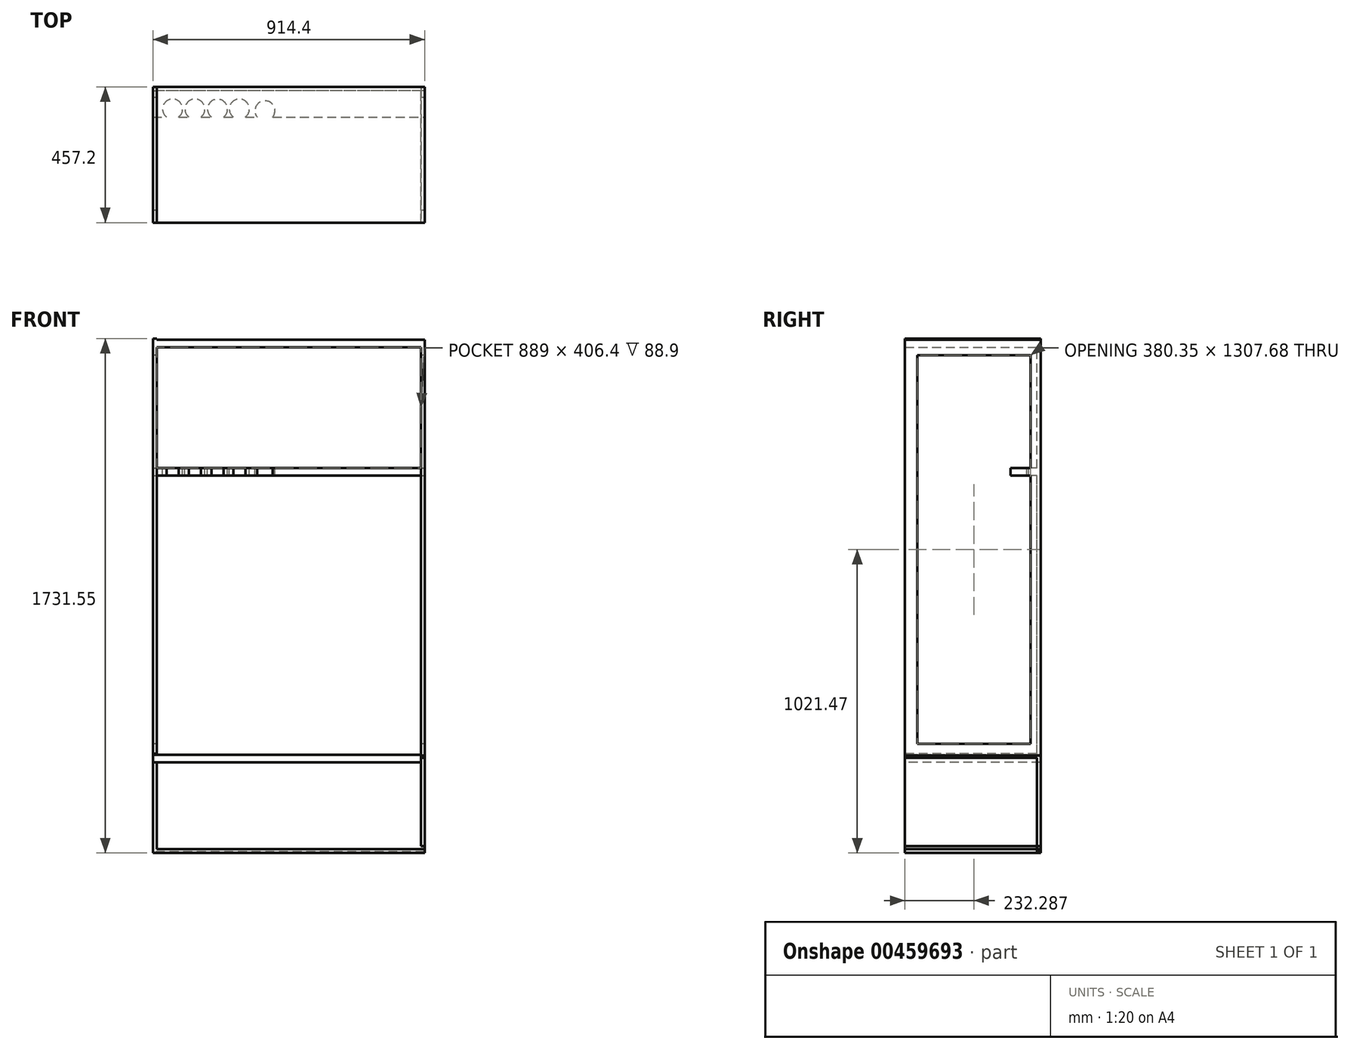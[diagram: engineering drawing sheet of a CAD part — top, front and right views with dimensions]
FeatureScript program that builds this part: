
annotation { "Feature Type Name" : "Feature", "Feature Type Description" : "" }
export const myFeature = defineFeature(function(context is Context, id is Id, definition is map)
    precondition{}
    {
        {
            var Q0;
            Q0=qCreatedBy(makeId("Top.planeOp"),FACE);
            var sketch = newSketch(context, id + "F0", { "sketchPlane" : qUnion([Q0])});
            skLineSegment(sketch, "E0.bottom", {"start": v(0, 0) * mm, "end": v(914.4, 0) * mm});
            skLineSegment(sketch, "E0.top", {"start": v(0, -457.2) * mm, "end": v(914.4, -457.2) * mm});
            skLineSegment(sketch, "E0.left", {"start": v(0, 0) * mm, "end": v(0, -457.2) * mm});
            skLineSegment(sketch, "E0.right", {"start": v(914.4, 0) * mm, "end": v(914.4, -457.2) * mm});
            skSolve(sketch);
        }
        {
            var Q0;
            Q0=makeQuery(id+"F0.imprint","IMPRINT",FACE,{"disambiguationData":[TD([[makeQuery(id+"F0.imprint","IMPRINT",EDGE,{"derivedFrom":sQuery(id+"F0.wireOp",EDGE,"E0.bottom")}),-1.0]])]});
            extrude(context, id + "F1", {"entities" : qUnion([Q0]), "depth" : 12.7 * mm});
        }
        {
            var Q0;
            Q0=qCreatedBy(makeId("Right.planeOp"),FACE);
            var sketch = newSketch(context, id + "F2", { "sketchPlane" : qUnion([Q0])});
            skLineSegment(sketch, "E1.bottom", {"start": v(0, 0) * mm, "end": v(-457.2, 0) * mm});
            skLineSegment(sketch, "E1.top", {"start": v(0, 304.8) * mm, "end": v(-457.2, 304.8) * mm});
            skLineSegment(sketch, "E1.left", {"start": v(0, 0) * mm, "end": v(0, 304.8) * mm});
            skLineSegment(sketch, "E1.right", {"start": v(-457.2, 0) * mm, "end": v(-457.2, 304.8) * mm});
            skSolve(sketch);
        }
        {
            var Q0;
            Q0=makeQuery(id+"F2.imprint","IMPRINT",FACE,{"disambiguationData":[TD([[makeQuery(id+"F2.imprint","IMPRINT",EDGE,{"derivedFrom":sQuery(id+"F2.wireOp",EDGE,"E1.bottom")}),-1.0]])]});
            extrude(context, id + "F3", {"entities" : qUnion([Q0]), "operationType" : NewBodyOperationType.ADD, "depth" : 12.7 * mm});
        }
        {
            var Q0;
            Q0=qCreatedBy(makeId("Right.planeOp"),FACE);
            cPlane(context, id + "F4", {"entities" : qUnion([Q0]), "cplaneType" : CPlaneType.OFFSET, "offset" : 914.4 * mm, "width" : 152.4 * mm, "height" : 152.4 * mm});
        }
        {
            var Q0;
            Q0=qCreatedBy(id+"F4.planeOp",FACE);
            var sketch = newSketch(context, id + "F5", { "sketchPlane" : qUnion([Q0])});
            skLineSegment(sketch, "E2.bottom", {"start": v(-457.2, 23.7) * mm, "end": v(0, 23.7) * mm});
            skLineSegment(sketch, "E2.top", {"start": v(-457.2, 328.5) * mm, "end": v(0, 328.5) * mm});
            skLineSegment(sketch, "E2.left", {"start": v(-457.2, 23.7) * mm, "end": v(-457.2, 328.5) * mm});
            skLineSegment(sketch, "E2.right", {"start": v(0, 23.7) * mm, "end": v(0, 328.5) * mm});
            skSolve(sketch);
        }
        {
            var Q0;
            Q0=makeQuery(id+"F5.imprint","IMPRINT",FACE,{"disambiguationData":[TD([[makeQuery(id+"F5.imprint","IMPRINT",EDGE,{"derivedFrom":sQuery(id+"F5.wireOp",EDGE,"E2.bottom")}),1.0]])]});
            extrude(context, id + "F6", {"entities" : qUnion([Q0]), "operationType" : NewBodyOperationType.ADD, "oppositeDirection" : true, "depth" : 12.7 * mm});
        }
        {
            var Q0;
            Q0=qCreatedBy(makeId("Top.planeOp"),FACE);
            cPlane(context, id + "F7", {"entities" : qUnion([Q0]), "cplaneType" : CPlaneType.OFFSET, "offset" : 304.8 * mm, "width" : 152.4 * mm, "height" : 152.4 * mm});
        }
        {
            var Q0;
            Q0=qCreatedBy(id+"F7.planeOp",FACE);
            var sketch = newSketch(context, id + "F8", { "sketchPlane" : qUnion([Q0])});
            skLineSegment(sketch, "E3.bottom", {"start": v(0, 0) * mm, "end": v(913.97, 0) * mm});
            skLineSegment(sketch, "E3.top", {"start": v(0, -456.64) * mm, "end": v(913.97, -456.64) * mm});
            skLineSegment(sketch, "E3.left", {"start": v(0, 0) * mm, "end": v(0, -456.64) * mm});
            skLineSegment(sketch, "E3.right", {"start": v(913.97, 0) * mm, "end": v(913.97, -456.64) * mm});
            skSolve(sketch);
        }
        {
            var Q0;
            Q0=makeQuery(id+"F8.imprint","IMPRINT",FACE,{"disambiguationData":[TD([[makeQuery(id+"F8.imprint","IMPRINT",EDGE,{"derivedFrom":sQuery(id+"F8.wireOp",EDGE,"E3.bottom")}),-1.0]])]});
            extrude(context, id + "F9", {"entities" : qUnion([Q0]), "operationType" : NewBodyOperationType.ADD, "depth" : 25.4 * mm});
        }
        {
            var Q0;
            Q0=qCreatedBy(makeId("Front.planeOp"),FACE);
            var sketch = newSketch(context, id + "F10", { "sketchPlane" : qUnion([Q0])});
            skLineSegment(sketch, "E4.bottom", {"start": v(914.4, 4.86) * mm, "end": v(0, 4.86) * mm});
            skLineSegment(sketch, "E4.top", {"start": v(914.4, 1706.66) * mm, "end": v(0, 1706.66) * mm});
            skLineSegment(sketch, "E4.left", {"start": v(914.4, 4.86) * mm, "end": v(914.4, 1706.66) * mm});
            skLineSegment(sketch, "E4.right", {"start": v(0, 4.86) * mm, "end": v(0, 1706.66) * mm});
            skSolve(sketch);
        }
        {
            var Q0;
            Q0 = qSketchRegion(id + "F10", true);
            extrude(context, id + "F11", {"entities" : qUnion([Q0]), "depth" : 12.7 * mm});
        }
        {
            var Q0;
            Q0=qCreatedBy(makeId("Top.planeOp"),FACE);
            cPlane(context, id + "F12", {"entities" : qUnion([Q0]), "cplaneType" : CPlaneType.OFFSET, "offset" : 1701.8 * mm, "width" : 152.4 * mm, "height" : 152.4 * mm});
        }
        {
            var Q0;
            Q0=qCreatedBy(id+"F12.planeOp",FACE);
            var sketch = newSketch(context, id + "F13", { "sketchPlane" : qUnion([Q0])});
            skLineSegment(sketch, "E5.bottom", {"start": v(0, 0) * mm, "end": v(914.4, 0) * mm});
            skLineSegment(sketch, "E5.top", {"start": v(0, -457.2) * mm, "end": v(914.4, -457.2) * mm});
            skLineSegment(sketch, "E5.left", {"start": v(0, 0) * mm, "end": v(0, -457.2) * mm});
            skLineSegment(sketch, "E5.right", {"start": v(914.4, 0) * mm, "end": v(914.4, -457.2) * mm});
            skSolve(sketch);
        }
        {
            var Q0;
            Q0 = qSketchRegion(id + "F13", true);
            extrude(context, id + "F14", {"entities" : qUnion([Q0]), "operationType" : NewBodyOperationType.ADD, "depth" : 25.4 * mm});
        }
        {
            var Q0;
            Q0=qCreatedBy(id+"F4.planeOp",FACE);
            var sketch = newSketch(context, id + "F15", { "sketchPlane" : qUnion([Q0])});
            skLineSegment(sketch, "E6.bottom", {"start": v(0, 1718.04) * mm, "end": v(-457.2, 1718.04) * mm});
            skLineSegment(sketch, "E6.top", {"start": v(0, 321.04) * mm, "end": v(-457.2, 321.04) * mm});
            skLineSegment(sketch, "E6.left", {"start": v(0, 1718.04) * mm, "end": v(0, 321.04) * mm});
            skLineSegment(sketch, "E6.right", {"start": v(-457.2, 1718.04) * mm, "end": v(-457.2, 321.04) * mm});
            skPoint(sketch, "E6.middle", {"position": v(-228.6, 1019.54) * mm});
            skSolve(sketch);
        }
        {
            var Q0;
            Q0=makeQuery(id+"F15.imprint","IMPRINT",FACE,{"disambiguationData":[TD([[makeQuery(id+"F15.imprint","IMPRINT",EDGE,{"derivedFrom":sQuery(id+"F15.wireOp",EDGE,"E6.bottom")}),1.0]])]});
            extrude(context, id + "F16", {"entities" : qUnion([Q0]), "oppositeDirection" : true, "depth" : 12.7 * mm});
        }
        {
            var Q0;
            Q0=qCreatedBy(id+"F4.planeOp",FACE);
            var sketch = newSketch(context, id + "F17", { "sketchPlane" : qUnion([Q0])});
            skLineSegment(sketch, "E7.bottom", {"start": v(-412.74, 1645.8) * mm, "end": v(-54.99, 1645.8) * mm});
            skLineSegment(sketch, "E7.top", {"start": v(-412.74, 384.63) * mm, "end": v(-54.99, 384.63) * mm});
            skLineSegment(sketch, "E7.left", {"start": v(-412.74, 1645.8) * mm, "end": v(-412.74, 384.63) * mm});
            skLineSegment(sketch, "E7.right", {"start": v(-54.99, 1645.8) * mm, "end": v(-54.99, 384.63) * mm});
            skSolve(sketch);
        }
        {
            var Q0;
            Q0 = qSketchRegion(id + "F17", true);
            extrude(context, id + "F18", {"entities" : qUnion([Q0]), "operationType" : NewBodyOperationType.REMOVE, "endBound" : BoundingType.THROUGH_ALL, "oppositeDirection" : true, "depth" : 25.4 * mm});
        }
        {
            var Q0;
            Q0=qCreatedBy(makeId("Right.planeOp"),FACE);
            var sketch = newSketch(context, id + "F19", { "sketchPlane" : qUnion([Q0])});
            skLineSegment(sketch, "E8.bottom", {"start": v(0, 1731.55) * mm, "end": v(-457.2, 1731.55) * mm});
            skLineSegment(sketch, "E8.top", {"start": v(0, 334.55) * mm, "end": v(-457.2, 334.55) * mm});
            skLineSegment(sketch, "E8.left", {"start": v(0, 1731.55) * mm, "end": v(0, 334.55) * mm});
            skLineSegment(sketch, "E8.right", {"start": v(-457.2, 1731.55) * mm, "end": v(-457.2, 334.55) * mm});
            skSolve(sketch);
        }
        {
            var Q0;
            Q0 = qSketchRegion(id + "F19", true);
            extrude(context, id + "F20", {"entities" : qUnion([Q0]), "operationType" : NewBodyOperationType.ADD, "depth" : 12.7 * mm});
        }
        {
            var Q0;
            Q0=qCreatedBy(makeId("Right.planeOp"),FACE);
            var sketch = newSketch(context, id + "F21", { "sketchPlane" : qUnion([Q0])});
            skLineSegment(sketch, "E9.bottom", {"start": v(-34.74, 1675.31) * mm, "end": v(-415.09, 1675.31) * mm});
            skLineSegment(sketch, "E9.top", {"start": v(-34.74, 367.63) * mm, "end": v(-415.09, 367.63) * mm});
            skLineSegment(sketch, "E9.left", {"start": v(-34.74, 1675.31) * mm, "end": v(-34.74, 367.63) * mm});
            skLineSegment(sketch, "E9.right", {"start": v(-415.09, 1675.31) * mm, "end": v(-415.09, 367.63) * mm});
            skSolve(sketch);
        }
        {
            var Q0;
            Q0 = qSketchRegion(id + "F21", true);
            extrude(context, id + "F22", {"entities" : qUnion([Q0]), "operationType" : NewBodyOperationType.REMOVE, "endBound" : BoundingType.THROUGH_ALL, "depth" : 25.4 * mm});
        }
        {
            var Q0;
            Q0=qCreatedBy(id+"F12.planeOp",FACE);
            cPlane(context, id + "F23", {"entities" : qUnion([Q0]), "cplaneType" : CPlaneType.OFFSET, "offset" : 431.8 * mm, "oppositeDirection" : true, "width" : 152.4 * mm, "height" : 152.4 * mm});
        }
        {
            var Q0;
            Q0=qCreatedBy(id+"F23.planeOp",FACE);
            var sketch = newSketch(context, id + "F24", { "sketchPlane" : qUnion([Q0])});
            skLineSegment(sketch, "E10.bottom", {"start": v(0, 0) * mm, "end": v(914.4, 0) * mm});
            skLineSegment(sketch, "E10.top", {"start": v(0, -101.6) * mm, "end": v(914.4, -101.6) * mm});
            skLineSegment(sketch, "E10.left", {"start": v(0, 0) * mm, "end": v(0, -101.6) * mm});
            skLineSegment(sketch, "E10.right", {"start": v(914.4, 0) * mm, "end": v(914.4, -101.6) * mm});
            skSolve(sketch);
        }
        {
            var Q0;
            Q0 = qSketchRegion(id + "F24", true);
            extrude(context, id + "F25", {"entities" : qUnion([Q0]), "operationType" : NewBodyOperationType.ADD, "depth" : 25.4 * mm});
        }
        {
            var Q0;
            Q0=makeQuery(id+"F25.opExtrude","CAP_FACE",FACE,{"disambiguationData":[OSD([sQuery(id+"F24.wireOp",EDGE,"E10.bottom"),sQuery(id+"F24.wireOp",EDGE,"E10.top"),sQuery(id+"F24.wireOp",EDGE,"E10.left"),sQuery(id+"F24.wireOp",EDGE,"E10.right")])],"isStart":false});
            var sketch = newSketch(context, id + "F26", { "sketchPlane" : qUnion([Q0])});
            skArc(sketch, "E11", {"start": v(86.68, -101.6) * mm, "mid": v(66.47, -41.06) * mm, "end": v(46.25, -101.6) * mm});
            skSolve(sketch);
        }
        {
            var Q0;
            {var subQ0=sQuery(id+"F26.wireOp",EDGE,"E11");Q0=makeQuery(id+"F26.imprint","IMPRINT",FACE,{"disambiguationData":[TD([[makeQuery(id+"F26.imprint","IMPRINT",EDGE,{"derivedFrom":subQ0}),1.0]])]});}
            extrude(context, id + "F27", {"entities" : qUnion([Q0]), "operationType" : NewBodyOperationType.REMOVE, "oppositeDirection" : true, "depth" : 25.4 * mm});
        }
        {
            var Q0;
            Q0=makeQuery(id+"F25.opExtrude","CAP_FACE",FACE,{"disambiguationData":[OSD([sQuery(id+"F24.wireOp",EDGE,"E10.bottom"),sQuery(id+"F24.wireOp",EDGE,"E10.top"),sQuery(id+"F24.wireOp",EDGE,"E10.left"),sQuery(id+"F24.wireOp",EDGE,"E10.right")])],"isStart":false});
            var sketch = newSketch(context, id + "F28", { "sketchPlane" : qUnion([Q0])});
            skArc(sketch, "E12", {"start": v(161.67, -101.6) * mm, "mid": v(141.45, -41.06) * mm, "end": v(121.23, -101.6) * mm});
            skSolve(sketch);
        }
        {
            var Q0;
            {var subQ0=sQuery(id+"F28.wireOp",EDGE,"E12");Q0=makeQuery(id+"F28.imprint","IMPRINT",FACE,{"disambiguationData":[TD([[makeQuery(id+"F28.imprint","IMPRINT",EDGE,{"derivedFrom":subQ0}),1.0]])]});}
            extrude(context, id + "F29", {"entities" : qUnion([Q0]), "operationType" : NewBodyOperationType.REMOVE, "oppositeDirection" : true, "depth" : 25.4 * mm});
        }
        {
            var Q0;
            Q0=makeQuery(id+"F25.opExtrude","CAP_FACE",FACE,{"disambiguationData":[OSD([sQuery(id+"F24.wireOp",EDGE,"E10.bottom"),sQuery(id+"F24.wireOp",EDGE,"E10.top"),sQuery(id+"F24.wireOp",EDGE,"E10.left"),sQuery(id+"F24.wireOp",EDGE,"E10.right")])],"isStart":false});
            var sketch = newSketch(context, id + "F30", { "sketchPlane" : qUnion([Q0])});
            skArc(sketch, "E13", {"start": v(237.8, -101.85) * mm, "mid": v(217.58, -41.32) * mm, "end": v(197.37, -101.85) * mm});
            skSolve(sketch);
        }
        {
            var Q0;
            {var subQ0=sQuery(id+"F30.wireOp",EDGE,"E13");var subQ1=sQuery(id+"F24.wireOp",EDGE,"E10.top");var subQ6=makeQuery(id+"F11.opExtrude","SWEPT_FACE",FACE,{"disambiguationData":[OSD([sQuery(id+"F10.wireOp",EDGE,"E4.left")])]});var subQ8=makeQuery(id+"F29.boolean.opBoolean","SPLIT",EDGE,{"disambiguationData":[TD([subQ6])],"derivedFrom":makeQuery(id+"F27.boolean.opBoolean","SPLIT",EDGE,{"disambiguationData":[TD([subQ6])],"derivedFrom":makeQuery(id+"F25.opExtrude","CAP_EDGE",EDGE,{"disambiguationData":[OSD([subQ1])],"isStart":false})})});var subQ9=makeQuery(id+"F30.imprint","INTERSECT",VERTEX,{"disambiguationData":[OD(0.0)],"derivedFrom":[subQ8,subQ0]});Q0=makeQuery(id+"F30.imprint","IMPRINT",FACE,{"disambiguationData":[TD([[makeQuery(id+"F30.imprint","IMPRINT",EDGE,{"disambiguationData":[TD([[subQ9,-1.0]])],"derivedFrom":subQ0}),1.0]])]});}
            extrude(context, id + "F31", {"entities" : qUnion([Q0]), "operationType" : NewBodyOperationType.REMOVE, "oppositeDirection" : true, "depth" : 25.4 * mm});
        }
        {
            var Q0;
            Q0=makeQuery(id+"F25.opExtrude","CAP_FACE",FACE,{"disambiguationData":[OSD([sQuery(id+"F24.wireOp",EDGE,"E10.bottom"),sQuery(id+"F24.wireOp",EDGE,"E10.top"),sQuery(id+"F24.wireOp",EDGE,"E10.left"),sQuery(id+"F24.wireOp",EDGE,"E10.right")])],"isStart":false});
            var sketch = newSketch(context, id + "F32", { "sketchPlane" : qUnion([Q0])});
            skArc(sketch, "E14", {"start": v(311.26, -101.6) * mm, "mid": v(291.04, -41.06) * mm, "end": v(270.83, -101.6) * mm});
            skSolve(sketch);
        }
        {
            var Q0;
            {var subQ0=sQuery(id+"F32.wireOp",EDGE,"E14");Q0=makeQuery(id+"F32.imprint","IMPRINT",FACE,{"disambiguationData":[TD([[makeQuery(id+"F32.imprint","IMPRINT",EDGE,{"derivedFrom":subQ0}),1.0]])]});}
            extrude(context, id + "F33", {"entities" : qUnion([Q0]), "operationType" : NewBodyOperationType.REMOVE, "oppositeDirection" : true, "depth" : 25.4 * mm});
        }
        {
            var Q0;
            Q0=makeQuery(id+"F25.opExtrude","CAP_FACE",FACE,{"disambiguationData":[OSD([sQuery(id+"F24.wireOp",EDGE,"E10.bottom"),sQuery(id+"F24.wireOp",EDGE,"E10.top"),sQuery(id+"F24.wireOp",EDGE,"E10.left"),sQuery(id+"F24.wireOp",EDGE,"E10.right")])],"isStart":false});
            var sketch = newSketch(context, id + "F34", { "sketchPlane" : qUnion([Q0])});
            skArc(sketch, "E15", {"start": v(397.33, -107.07) * mm, "mid": v(377.12, -46.53) * mm, "end": v(356.9, -107.07) * mm});
            skSolve(sketch);
        }
        {
            var Q0;
            {var subQ0=sQuery(id+"F34.wireOp",EDGE,"E15");var subQ1=sQuery(id+"F24.wireOp",EDGE,"E10.top");var subQ6=makeQuery(id+"F11.opExtrude","SWEPT_FACE",FACE,{"disambiguationData":[OSD([sQuery(id+"F10.wireOp",EDGE,"E4.left")])]});var subQ8=makeQuery(id+"F33.boolean.opBoolean","SPLIT",EDGE,{"disambiguationData":[TD([subQ6])],"derivedFrom":makeQuery(id+"F31.boolean.opBoolean","SPLIT",EDGE,{"disambiguationData":[TD([subQ6])],"derivedFrom":makeQuery(id+"F29.boolean.opBoolean","SPLIT",EDGE,{"disambiguationData":[TD([subQ6])],"derivedFrom":makeQuery(id+"F27.boolean.opBoolean","SPLIT",EDGE,{"disambiguationData":[TD([subQ6])],"derivedFrom":makeQuery(id+"F25.opExtrude","CAP_EDGE",EDGE,{"disambiguationData":[OSD([subQ1])],"isStart":false})})})})});var subQ9=makeQuery(id+"F34.imprint","INTERSECT",VERTEX,{"disambiguationData":[OD(0.0)],"derivedFrom":[subQ8,subQ0]});Q0=makeQuery(id+"F34.imprint","IMPRINT",FACE,{"disambiguationData":[TD([[makeQuery(id+"F34.imprint","IMPRINT",EDGE,{"disambiguationData":[TD([[subQ9,-1.0]])],"derivedFrom":subQ0}),1.0]])]});}
            extrude(context, id + "F35", {"entities" : qUnion([Q0]), "operationType" : NewBodyOperationType.REMOVE, "oppositeDirection" : true, "depth" : 25.4 * mm});
        }
    });
